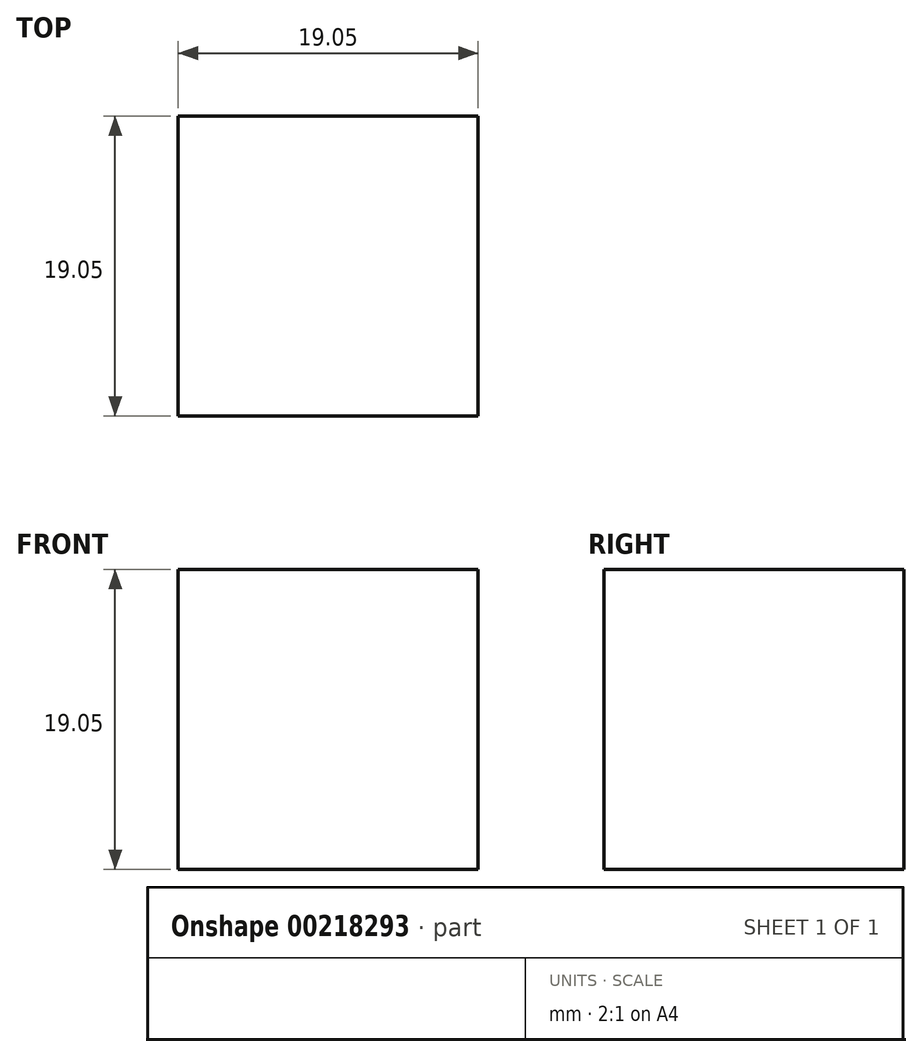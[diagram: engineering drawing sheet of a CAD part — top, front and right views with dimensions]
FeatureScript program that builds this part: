
annotation { "Feature Type Name" : "Feature", "Feature Type Description" : "" }
export const myFeature = defineFeature(function(context is Context, id is Id, definition is map)
    precondition{}
    {
        {
            var Q0;
            Q0=qCreatedBy(makeId("Front.planeOp"),FACE);
            var sketch = newSketch(context, id + "F0", { "sketchPlane" : qUnion([Q0])});
            skLineSegment(sketch, "E0", {"start": v(-69.95, 35.45) * mm, "end": v(-50.9, 35.45) * mm});
            skLineSegment(sketch, "E1", {"start": v(-50.9, 35.45) * mm, "end": v(-50.9, 16.4) * mm});
            skLineSegment(sketch, "E2", {"start": v(-50.9, 16.4) * mm, "end": v(-69.95, 16.4) * mm});
            skLineSegment(sketch, "E3", {"start": v(-69.95, 16.4) * mm, "end": v(-69.95, 35.45) * mm});
            skSolve(sketch);
        }
        {
            var Q0;
            Q0=makeQuery(id+"F0.imprint","IMPRINT",FACE,{"disambiguationData":[TD([[makeQuery(id+"F0.imprint","IMPRINT",EDGE,{"derivedFrom":sQuery(id+"F0.wireOp",EDGE,"E0")}),-1.0]])]});
            extrude(context, id + "F1", {"entities" : qUnion([Q0]), "depth" : 19.05 * mm});
        }
    });
